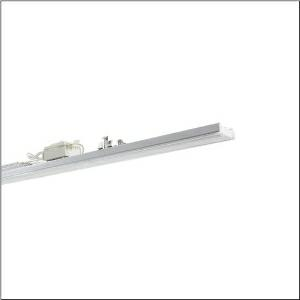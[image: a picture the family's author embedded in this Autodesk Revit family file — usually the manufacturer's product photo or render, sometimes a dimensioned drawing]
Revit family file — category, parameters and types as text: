
# Revit family: licross_21_recessed_mo_52tl18dv4e5g
name_source: partatom
category: Lighting Fixtures
units: mm (PartAtom-declared; Revit-internal decimal feet)

## family parameters
Cut with Voids When Loaded = No
Host = Face
Light Source = No
Part Type = Normal
Room Calculation Point = No
Round Connector Dimension = Use Diameter
Shared = No

## types (1)
- --- (1 x LED, 14980 lm, 85.3 W, 4000K)
    Apparent Load = 85 VA
    CIE Flux Codes = 79 95 99 100 100
    Color Rendering = 80
    Color Temperature = 4000K
    Default Elevation = 1800 mm
    Description = Licross 21 Recessed MO, luminaire insert, of sheet steel, galvanised, coil coated, white, length: 2.250mm, width: 66mm, height: 67mm, LED rated luminous flux: 14.980lm, light colour: 840, SDCM (Standard Deviation of Colour Matching)MacAdam ≤ 3 SDCM (initial), control gear: DALI 2, with plug, 5-pole, with phase selection, mains connection: 220..240V, AC, 50/60Hz, rated input power: 85W, internal wiring halogen-free, primary light control with lens, of plastic, primary optical cover: cover, of PMMA, light emission: direct distribution, primary light characteristic: symmetric, protection rating (complete): IP40, insulation class (complete): insulation class I (protective earthing), certification: CE, ENEC, VDE, UKCA, protection symbol: D if used in an environment without relevant dust loads with corresponding accessories, impact resistance: IK06, permissible ambient temperature for indoor applications: -25..+35°C, corresponds to IFS (International Featured Standards) requirements for safety and quality in the food industry, reducing of maximum allowable ambient temperature of 5°C with ceiling mounting, LABS conformity tested according to VDMA 24364:2018-05, The light source and the operating device comply with the requirements of the Ecodesign Regulation (EU) 2019/2020 and are replaceable in accordance with this regulation, packaging unit: 1 piece
    Height = 58 mm
    Lamp = 1 x LED
    Lamp Light Flux = 14980 lm
    Lamp Power = 85.3 W
    Lamp count = 1
    Length = 2250 mm
    Luminous efficacy = 176 lm/W
    Manufacturer = Siteco
    ModVariant = No
    Model = 52TL18DV4E5G
    Mounting Place = Ceiling
    Mounting Type = Pendant
    Number of Poles = 1
    OnlyDefault = Yes
    Power Factor = 1
    Product Name = Licross 21 Recessed MO
    Product group = luminaire insert | ceiling pendant
    ProductGroupID = 901
    Protection Class = Protection class I
    Protection Degree = IP 40
    RLX_Detail_Level = 1
    RLX_Emergency_Light_Flux = 0 lm
    RLX_Emergency_Type = 0
    RLX_Emergency_Type_DB = No
    RlxData = <blob elided: 29809 chars, md5=f76c1c68>
    Socket = socket
    Standby Power = 0 W
    System Light Flux = 14980 lm
    System Power = 85 W
    Type Comments = factory setting: luminous flux: 100 % | dim-lin: 254 | 390 mA
    Type Image = l_1296930.jpg
    URL = http://relux.com
    VarID = @adj_126217
    Voltage = 0 V
    Weight = 0.00 kg
    Width = 66 mm

## geometry (parser evidence)
native form markers: Blend x4, Sweep x10
no freeform markers — native parametric forms only
